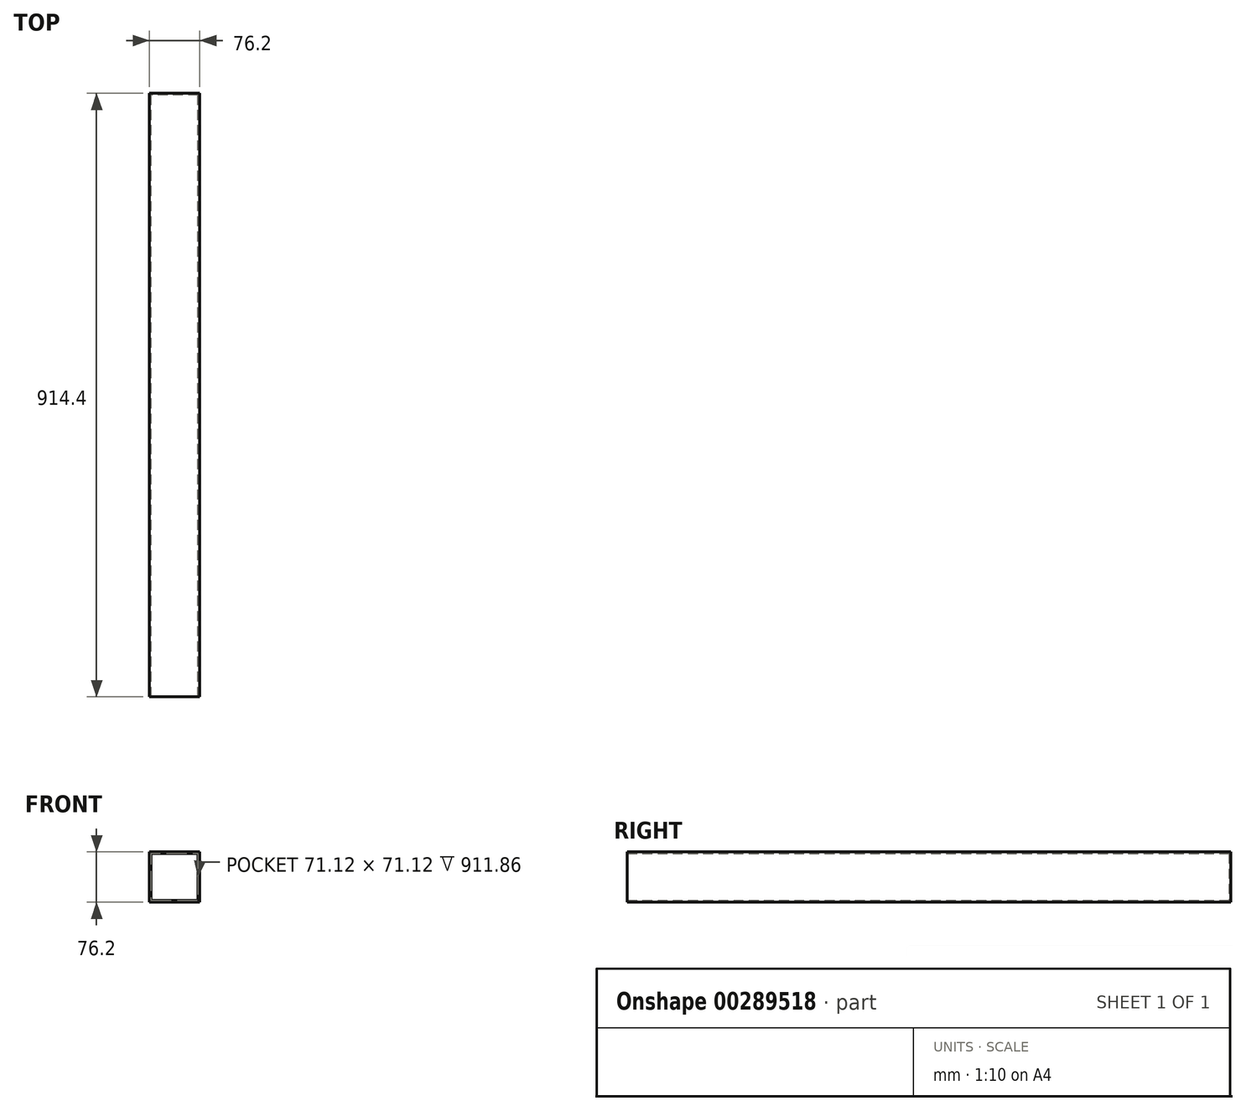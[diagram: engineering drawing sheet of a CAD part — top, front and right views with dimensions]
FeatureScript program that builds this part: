
annotation { "Feature Type Name" : "Feature", "Feature Type Description" : "" }
export const myFeature = defineFeature(function(context is Context, id is Id, definition is map)
    precondition{}
    {
        {
            var Q0;
            Q0=qCreatedBy(makeId("Front.planeOp"),FACE);
            var sketch = newSketch(context, id + "F0", { "sketchPlane" : qUnion([Q0])});
            skLineSegment(sketch, "E0.bottom", {"start": v(38.1, 38.1) * mm, "end": v(-38.1, 38.1) * mm});
            skLineSegment(sketch, "E0.top", {"start": v(38.1, -38.1) * mm, "end": v(-38.1, -38.1) * mm});
            skLineSegment(sketch, "E0.left", {"start": v(38.1, 38.1) * mm, "end": v(38.1, -38.1) * mm});
            skLineSegment(sketch, "E0.right", {"start": v(-38.1, 38.1) * mm, "end": v(-38.1, -38.1) * mm});
            skPoint(sketch, "E0.middle", {"position": v(0, 0) * mm});
            skSolve(sketch);
        }
        {
            var Q0;
            Q0=qSketchRegion(id+"F0",true);
            extrude(context, id + "F1", {"entities" : qUnion([Q0]), "depth" : 914.4 * mm});
        }
        {
            var Q0;
            Q0=makeQuery(id+"F1.opExtrude","CAP_FACE",FACE,{"disambiguationData":[OSD([sQuery(id+"F0.wireOp",EDGE,"E0.bottom"),sQuery(id+"F0.wireOp",EDGE,"E0.top"),sQuery(id+"F0.wireOp",EDGE,"E0.left"),sQuery(id+"F0.wireOp",EDGE,"E0.right")])],"isStart":false});
            shell(context, id + "F2", {"entities" : qUnion([Q0]), "thickness" : 2.54 * mm});
        }
    });
